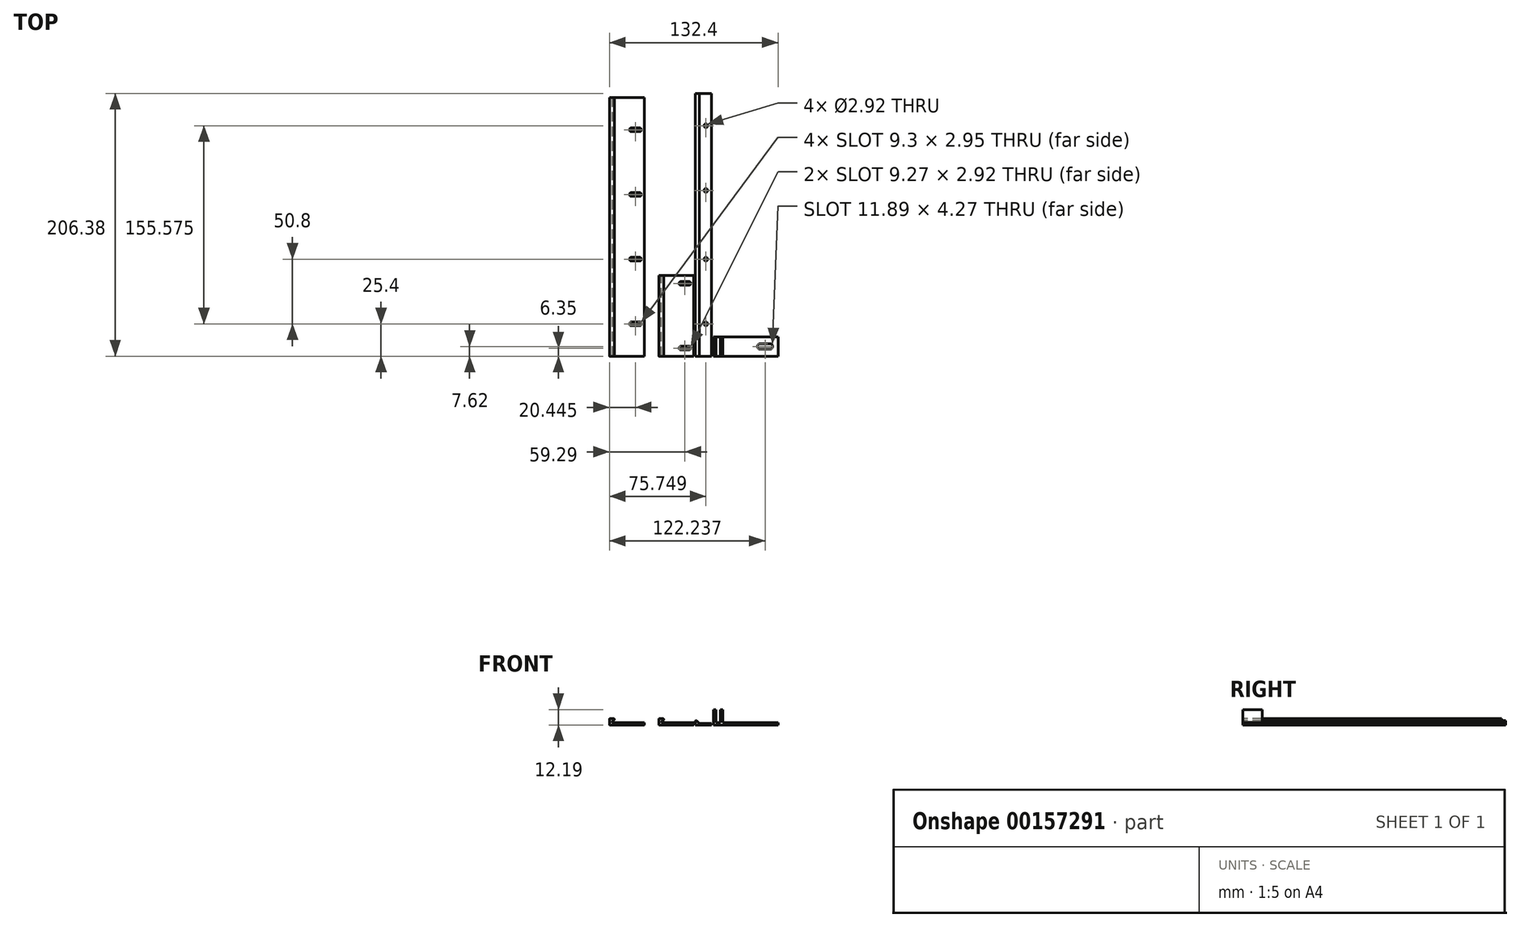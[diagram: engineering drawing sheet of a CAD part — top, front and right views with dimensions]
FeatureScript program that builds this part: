
annotation { "Feature Type Name" : "Feature", "Feature Type Description" : "" }
export const myFeature = defineFeature(function(context is Context, id is Id, definition is map)
    precondition{}
    {
        {
            var Q0;
            Q0=qCreatedBy(makeId("Top.planeOp"),FACE);
            var sketch = newSketch(context, id + "F0", { "sketchPlane" : qUnion([Q0])});
            skLineSegment(sketch, "E0.bottom", {"start": v(8.37, 0) * mm, "end": v(33.77, 0) * mm});
            skLineSegment(sketch, "E0.top", {"start": v(8.37, 63.5) * mm, "end": v(33.77, 63.5) * mm});
            skLineSegment(sketch, "E0.left", {"start": v(8.37, 0) * mm, "end": v(8.37, 63.5) * mm});
            skLineSegment(sketch, "E0.right", {"start": v(33.77, 0) * mm, "end": v(33.77, 63.5) * mm});
            skSolve(sketch);
        }
        {
            var Q0;
            Q0 = qSketchRegion(id + "F0", true);
            extrude(context, id + "F1", {"entities" : qUnion([Q0]), "depth" : 2.03 * mm});
        }
        {
            var Q0;
            Q0=makeQuery(id+"F1.opExtrude","SWEPT_FACE",FACE,{"disambiguationData":[OSD([sQuery(id+"F0.wireOp",EDGE,"E0.bottom")])]});
            var sketch = newSketch(context, id + "F2", { "sketchPlane" : qUnion([Q0])});
            skLineSegment(sketch, "E1.bottom", {"start": v(8.37, 0) * mm, "end": v(6.84, 0) * mm});
            skLineSegment(sketch, "E1.left", {"start": v(8.37, 0) * mm, "end": v(8.37, 2.54) * mm});
            skLineSegment(sketch, "E1.right", {"start": v(6.33, 0.5) * mm, "end": v(6.33, 4.57) * mm});
            skLineSegment(sketch, "E2", {"start": v(10.04, 4.21) * mm, "end": v(8.37, 2.54) * mm});
            skLineSegment(sketch, "E3", {"start": v(6.84, 5.08) * mm, "end": v(9.68, 5.08) * mm});
            skPoint(sketch, "E4.visualSharp", {"position": v(6.33, 5.08) * mm});
            skArc(sketch, "E4.filletArc", {"start": v(6.84, 5.08) * mm, "mid": v(6.48, 4.93) * mm, "end": v(6.33, 4.57) * mm});
            skPoint(sketch, "E5.visualSharp", {"position": v(6.33, 0) * mm});
            skArc(sketch, "E5.filletArc", {"start": v(6.33, 0.5) * mm, "mid": v(6.48, 0.15) * mm, "end": v(6.84, 0) * mm});
            skPoint(sketch, "E6.visualSharp", {"position": v(10.9, 5.08) * mm});
            skArc(sketch, "E6.filletArc", {"start": v(10.04, 4.21) * mm, "mid": v(10.15, 4.77) * mm, "end": v(9.68, 5.08) * mm});
            skSolve(sketch);
        }
        {
            var Q0;
            Q0 = qSketchRegion(id + "F2", true);
            extrude(context, id + "F3", {"entities" : qUnion([Q0]), "operationType" : NewBodyOperationType.ADD, "oppositeDirection" : true, "depth" : 63.5 * mm});
        }
        {
            var Q0;
            Q0=makeQuery(id+"F1.opExtrude","CAP_EDGE",EDGE,{"disambiguationData":[OSD([sQuery(id+"F0.wireOp",EDGE,"E0.right")])],"isStart":true});
            fillet(context, id + "F4", {"entities" : qUnion([Q0]), "radius" : 0.5 * mm, "allowEdgeOverflow" : false});
        }
        {
            var Q0;
            Q0=makeQuery(id+"F1.opExtrude","CAP_FACE",FACE,{"disambiguationData":[OSD([sQuery(id+"F0.wireOp",EDGE,"E0.bottom"),sQuery(id+"F0.wireOp",EDGE,"E0.top"),sQuery(id+"F0.wireOp",EDGE,"E0.left"),sQuery(id+"F0.wireOp",EDGE,"E0.right")])],"isStart":false});
            var sketch = newSketch(context, id + "F5", { "sketchPlane" : qUnion([Q0])});
            skArc(sketch, "E7", {"start": v(29.96, 4.89) * mm, "mid": v(31.42, 6.35) * mm, "end": v(29.96, 7.81) * mm});
            skArc(sketch, "E8", {"start": v(23.6, 7.81) * mm, "mid": v(22.14, 6.35) * mm, "end": v(23.6, 4.89) * mm});
            skLineSegment(sketch, "E9", {"start": v(23.6, 7.81) * mm, "end": v(29.96, 7.81) * mm});
            skLineSegment(sketch, "E10", {"start": v(29.96, 4.89) * mm, "end": v(23.6, 4.89) * mm});
            skArc(sketch, "E11", {"start": v(29.96, 55.69) * mm, "mid": v(31.42, 57.15) * mm, "end": v(29.96, 58.61) * mm});
            skArc(sketch, "E12", {"start": v(23.6, 58.61) * mm, "mid": v(22.14, 57.15) * mm, "end": v(23.6, 55.69) * mm});
            skLineSegment(sketch, "E13", {"start": v(23.6, 58.61) * mm, "end": v(29.96, 58.61) * mm});
            skLineSegment(sketch, "E14", {"start": v(29.96, 55.69) * mm, "end": v(23.6, 55.69) * mm});
            skSolve(sketch);
        }
        {
            var Q0;
            Q0 = qSketchRegion(id + "F5", true);
            extrude(context, id + "F6", {"entities" : qUnion([Q0]), "operationType" : NewBodyOperationType.REMOVE, "endBound" : BoundingType.UP_TO_NEXT, "oppositeDirection" : true, "depth" : 25.4 * mm});
        }
        {
            var Q0;
            Q0=qCreatedBy(makeId("Front.planeOp"),FACE);
            var sketch = newSketch(context, id + "F7", { "sketchPlane" : qUnion([Q0])});
            skLineSegment(sketch, "E15", {"start": v(34.98, 3.05) * mm, "end": v(34.98, 0) * mm});
            skLineSegment(sketch, "E16", {"start": v(34.98, 0) * mm, "end": v(47.68, 0) * mm});
            skLineSegment(sketch, "E17", {"start": v(47.68, 0) * mm, "end": v(47.68, 1.27) * mm});
            skLineSegment(sketch, "E18", {"start": v(47.68, 1.27) * mm, "end": v(37.99, 1.27) * mm});
            skLineSegment(sketch, "E19", {"start": v(37.99, 1.27) * mm, "end": v(35.85, 3.4) * mm});
            skPoint(sketch, "E20.visualSharp", {"position": v(34.98, 4.27) * mm});
            skArc(sketch, "E20.filletArc", {"start": v(35.85, 3.4) * mm, "mid": v(35.3, 3.52) * mm, "end": v(34.98, 3.05) * mm});
            skSolve(sketch);
        }
        {
            var Q0;
            Q0 = qSketchRegion(id + "F7", true);
            extrude(context, id + "F8", {"entities" : qUnion([Q0]), "oppositeDirection" : true, "depth" : 206.38 * mm});
        }
        {
            var Q0;
            Q0=makeQuery(id+"F8.opExtrude","SWEPT_FACE",FACE,{"disambiguationData":[OSD([sQuery(id+"F7.wireOp",EDGE,"E18")])]});
            var sketch = newSketch(context, id + "F9", { "sketchPlane" : qUnion([Q0])});
            skCircle(sketch, "E21", {"center": v(43.24, 180.98) * mm, "radius": 1.46 * mm});
            skCircle(sketch, "E22", {"center": v(43.24, 130.18) * mm, "radius": 1.46 * mm});
            skCircle(sketch, "E23", {"center": v(43.24, 76.2) * mm, "radius": 1.46 * mm});
            skCircle(sketch, "E24", {"center": v(43.24, 25.4) * mm, "radius": 1.46 * mm});
            skSolve(sketch);
        }
        {
            var Q0;
            Q0 = qSketchRegion(id + "F9", true);
            extrude(context, id + "F10", {"entities" : qUnion([Q0]), "operationType" : NewBodyOperationType.REMOVE, "endBound" : BoundingType.UP_TO_NEXT, "oppositeDirection" : true, "depth" : 25.4 * mm});
        }
        {
            var Q0;
            Q0=qCreatedBy(makeId("Front.planeOp"),FACE);
            var sketch = newSketch(context, id + "F11", { "sketchPlane" : qUnion([Q0])});
            skLineSegment(sketch, "E25", {"start": v(49.09, 0) * mm, "end": v(49.09, 12.2) * mm});
            skLineSegment(sketch, "E26", {"start": v(49.09, 12.2) * mm, "end": v(51.12, 12.2) * mm});
            skLineSegment(sketch, "E27", {"start": v(51.12, 12.2) * mm, "end": v(51.12, 2.03) * mm});
            skLineSegment(sketch, "E28", {"start": v(51.12, 2.03) * mm, "end": v(54.47, 2.03) * mm});
            skLineSegment(sketch, "E29", {"start": v(54.47, 2.03) * mm, "end": v(54.47, 12.2) * mm});
            skLineSegment(sketch, "E30", {"start": v(54.47, 12.2) * mm, "end": v(56.5, 12.2) * mm});
            skLineSegment(sketch, "E31", {"start": v(56.5, 12.2) * mm, "end": v(56.5, 2.03) * mm});
            skLineSegment(sketch, "E32", {"start": v(56.5, 2.03) * mm, "end": v(99.89, 2.03) * mm});
            skLineSegment(sketch, "E33", {"start": v(99.89, 2.03) * mm, "end": v(99.89, 0) * mm});
            skLineSegment(sketch, "E34", {"start": v(99.89, 0) * mm, "end": v(49.09, 0) * mm});
            skSolve(sketch);
        }
        {
            var Q0;
            Q0 = qSketchRegion(id + "F11", true);
            extrude(context, id + "F12", {"entities" : qUnion([Q0]), "oppositeDirection" : true, "depth" : 15.24 * mm});
        }
        {
            var Q0;
            Q0=makeQuery(id+"F12.opExtrude","SWEPT_FACE",FACE,{"disambiguationData":[OSD([sQuery(id+"F11.wireOp",EDGE,"E32")])]});
            var sketch = newSketch(context, id + "F13", { "sketchPlane" : qUnion([Q0])});
            skArc(sketch, "E35", {"start": v(85.92, 9.75) * mm, "mid": v(83.78, 7.62) * mm, "end": v(85.92, 5.49) * mm});
            skArc(sketch, "E36", {"start": v(93.54, 5.49) * mm, "mid": v(95.67, 7.62) * mm, "end": v(93.54, 9.75) * mm});
            skLineSegment(sketch, "E37", {"start": v(85.92, 9.75) * mm, "end": v(93.54, 9.75) * mm});
            skLineSegment(sketch, "E38", {"start": v(93.54, 5.49) * mm, "end": v(85.92, 5.49) * mm});
            skSolve(sketch);
        }
        {
            var Q0;
            Q0 = qSketchRegion(id + "F13", true);
            extrude(context, id + "F14", {"entities" : qUnion([Q0]), "operationType" : NewBodyOperationType.REMOVE, "endBound" : BoundingType.UP_TO_NEXT, "oppositeDirection" : true, "depth" : 25.4 * mm});
        }
        {
            var Q0;
            Q0=qCreatedBy(makeId("Front.planeOp"),FACE);
            var sketch = newSketch(context, id + "F15", { "sketchPlane" : qUnion([Q0])});
            skLineSegment(sketch, "E39", {"start": v(-5.59, 0) * mm, "end": v(-32, 0) * mm});
            skLineSegment(sketch, "E40", {"start": v(-32.51, 0.5) * mm, "end": v(-32.51, 4.57) * mm});
            skLineSegment(sketch, "E41", {"start": v(-32, 5.08) * mm, "end": v(-29.17, 5.08) * mm});
            skLineSegment(sketch, "E42", {"start": v(-28.8, 4.21) * mm, "end": v(-30.48, 2.54) * mm});
            skLineSegment(sketch, "E43", {"start": v(-30.48, 2.03) * mm, "end": v(-5.08, 2.03) * mm});
            skLineSegment(sketch, "E44", {"start": v(-5.08, 2.03) * mm, "end": v(-5.08, 0.5) * mm});
            skPoint(sketch, "E45.visualSharp", {"position": v(-32.51, 5.08) * mm});
            skArc(sketch, "E45.filletArc", {"start": v(-32, 5.08) * mm, "mid": v(-32.36, 4.93) * mm, "end": v(-32.51, 4.57) * mm});
            skPoint(sketch, "E46.visualSharp", {"position": v(-27.94, 5.08) * mm});
            skArc(sketch, "E46.filletArc", {"start": v(-28.8, 4.21) * mm, "mid": v(-28.7, 4.77) * mm, "end": v(-29.17, 5.08) * mm});
            skPoint(sketch, "E47.visualSharp", {"position": v(-32.51, 0) * mm});
            skArc(sketch, "E47.filletArc", {"start": v(-32.51, 0.5) * mm, "mid": v(-32.36, 0.15) * mm, "end": v(-32, 0) * mm});
            skPoint(sketch, "E48.visualSharp", {"position": v(-5.08, 0) * mm});
            skArc(sketch, "E48.filletArc", {"start": v(-5.59, 0) * mm, "mid": v(-5.23, 0.15) * mm, "end": v(-5.08, 0.5) * mm});
            skLineSegment(sketch, "E49", {"start": v(-30.48, 2.54) * mm, "end": v(-30.48, 2.03) * mm});
            skSolve(sketch);
        }
        {
            var Q0;
            Q0 = qSketchRegion(id + "F15", true);
            extrude(context, id + "F16", {"entities" : qUnion([Q0]), "oppositeDirection" : true, "depth" : 203.2 * mm});
        }
        {
            var Q0;
            Q0=makeQuery(id+"F16.opExtrude","SWEPT_FACE",FACE,{"disambiguationData":[OSD([sQuery(id+"F15.wireOp",EDGE,"E43")])]});
            var sketch = newSketch(context, id + "F17", { "sketchPlane" : qUnion([Q0])});
            skArc(sketch, "E50", {"start": v(-8.9, 23.93) * mm, "mid": v(-7.42, 25.4) * mm, "end": v(-8.9, 26.87) * mm});
            skArc(sketch, "E51", {"start": v(-15.24, 26.87) * mm, "mid": v(-16.71, 25.4) * mm, "end": v(-15.24, 23.93) * mm});
            skLineSegment(sketch, "E52", {"start": v(-15.24, 26.87) * mm, "end": v(-8.9, 26.87) * mm});
            skLineSegment(sketch, "E53", {"start": v(-8.9, 23.93) * mm, "end": v(-15.24, 23.93) * mm});
            skLineSegment(sketch, "E54.0.1.0", {"start": v(-8.9, 74.73) * mm, "end": v(-15.24, 74.73) * mm});
            skArc(sketch, "E54.0.1.1", {"start": v(-8.9, 74.73) * mm, "mid": v(-7.42, 76.2) * mm, "end": v(-8.9, 77.67) * mm});
            skLineSegment(sketch, "E54.0.1.2", {"start": v(-15.24, 77.67) * mm, "end": v(-8.9, 77.67) * mm});
            skArc(sketch, "E54.0.1.3", {"start": v(-15.24, 77.67) * mm, "mid": v(-16.71, 76.2) * mm, "end": v(-15.24, 74.73) * mm});
            skLineSegment(sketch, "E54.0.2.0", {"start": v(-8.9, 125.53) * mm, "end": v(-15.24, 125.53) * mm});
            skArc(sketch, "E54.0.2.1", {"start": v(-8.9, 125.53) * mm, "mid": v(-7.42, 127) * mm, "end": v(-8.9, 128.47) * mm});
            skLineSegment(sketch, "E54.0.2.2", {"start": v(-15.24, 128.47) * mm, "end": v(-8.9, 128.47) * mm});
            skArc(sketch, "E54.0.2.3", {"start": v(-15.24, 128.47) * mm, "mid": v(-16.71, 127) * mm, "end": v(-15.24, 125.53) * mm});
            skLineSegment(sketch, "E54.0.3.0", {"start": v(-8.9, 176.33) * mm, "end": v(-15.24, 176.33) * mm});
            skArc(sketch, "E54.0.3.1", {"start": v(-8.9, 176.33) * mm, "mid": v(-7.42, 177.8) * mm, "end": v(-8.9, 179.27) * mm});
            skLineSegment(sketch, "E54.0.3.2", {"start": v(-15.24, 179.27) * mm, "end": v(-8.9, 179.27) * mm});
            skArc(sketch, "E54.0.3.3", {"start": v(-15.24, 179.27) * mm, "mid": v(-16.71, 177.8) * mm, "end": v(-15.24, 176.33) * mm});
            skLineSegment(sketch, "E54.direction1", {"start": v(-15.24, 23.93) * mm, "end": v(10.16, 23.93) * mm, "construction": true});
            skLineSegment(sketch, "E54.direction2", {"start": v(-15.24, 23.93) * mm, "end": v(-15.24, 74.73) * mm, "construction": true});
            skSolve(sketch);
        }
        {
            var Q0;
            Q0 = qSketchRegion(id + "F17", true);
            extrude(context, id + "F18", {"entities" : qUnion([Q0]), "operationType" : NewBodyOperationType.REMOVE, "endBound" : BoundingType.UP_TO_NEXT, "oppositeDirection" : true, "depth" : 25.4 * mm});
        }
    });
